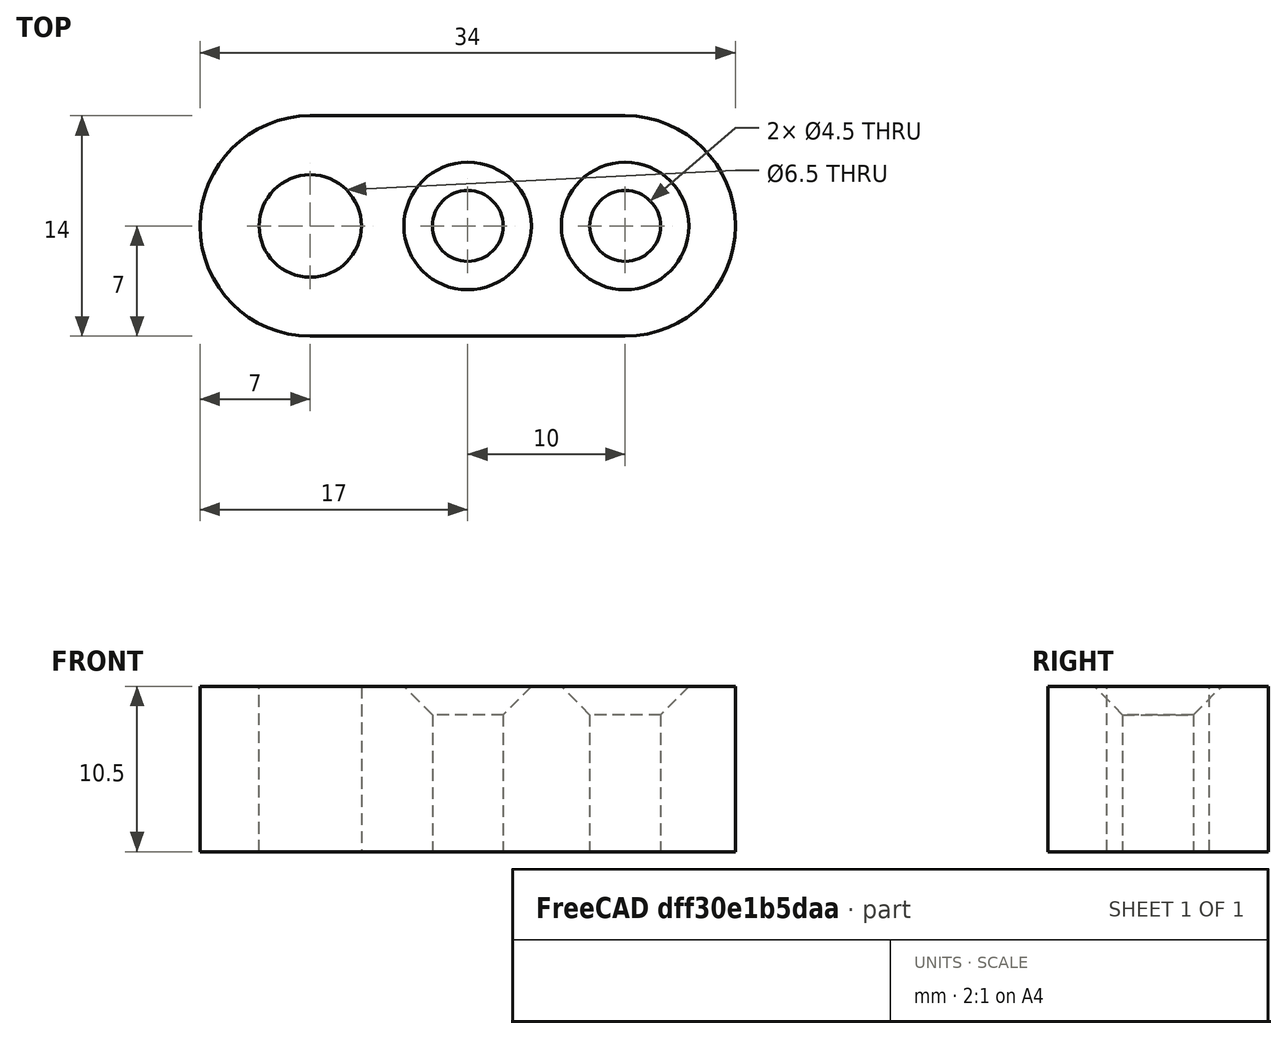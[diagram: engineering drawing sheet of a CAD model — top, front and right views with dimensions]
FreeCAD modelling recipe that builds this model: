
FCSTD DOCUMENT  (FreeCAD 0.19R24267 +99 (Git))
Label: topes
License: All rights reserved
LicenseURL: http://en.wikipedia.org/wiki/All_rights_reserved
objects: Sketcher::SketchObject×3, PartDesign::Pad×1, PartDesign::Hole×1, PartDesign::Pocket×1, PartDesign::Body×1, Mesh::Feature×1
note: 10 computed .brp shape members not serialized (recipe doc carries the construction recipe); baked Part::Feature solids carry a one-line shape summary decoded from their .brp

FEATURE [Sketcher::SketchObject] Sketch
  FullyConstrained = true
  MapMode = 5
  Support = -> [XY_Plane]
  sketch-geometry (4):
    g0: ArcOfCircle CenterX=0 CenterY=0 CenterZ=0 NormalX=0 NormalY=0 NormalZ=1 AngleXU=0 Radius=7 StartAngle=1.5708 EndAngle=4.71239
    g1: ArcOfCircle CenterX=20 CenterY=-4e-16 CenterZ=0 NormalX=0 NormalY=0 NormalZ=1 AngleXU=0 Radius=7 StartAngle=4.71239 EndAngle=7.85398
    g2: LineSegment StartX=-1.3e-15 StartY=-7 StartZ=0 EndX=20 EndY=-7 EndZ=0
    g3: LineSegment StartX=7.66e-14 StartY=7 StartZ=0 EndX=20 EndY=7 EndZ=0
  constraints (9):
    c: Tangent(g0,g3) = 1.5708
    c: Tangent(g0,g2) = -1.5708
    c: Tangent(g2,g1) = -1.5708
    c: Tangent(g3,g1) = 1.5708
    c: Horizontal(g2)
    c: Equal(g0,g1)
    c: Radius(g0) = 7
    c: Coincident(g0,g-1)
    c: DistanceX(g3,g3) = 20
FEATURE [PartDesign::Pad] Pad
  Direction = (1,1,1)
  Length = 10.5
  Length2 = 100
  Profile = -> Sketch
  Type = 0
FEATURE [Sketcher::SketchObject] Sketch001
  FullyConstrained = true
  MapMode = 5
  Placement = pos=(0,0,10.5) rot=(0,0,1;0rad)
  Support = -> [Pad]
  sketch-geometry (2):
    g0: Circle CenterX=10 CenterY=0 CenterZ=0 NormalX=0 NormalY=0 NormalZ=1 AngleXU=0 Radius=2
    g1: Circle CenterX=20 CenterY=0 CenterZ=0 NormalX=0 NormalY=0 NormalZ=1 AngleXU=0 Radius=2
  constraints (6):
    c: PointOnObject(g0,g-1)
    c: Diameter(g0) = 4
    c: Equal(g0,g1) = 4
    c: PointOnObject(g1,g-1)
    c: DistanceX(g0,g1) = 10
    c: DistanceX(g-1,g0) = 10
FEATURE [PartDesign::Hole] Hole
  BaseFeature = -> Pad
  Depth = 25
  DepthType = 1
  Diameter = 4.5
  DrillForDepth = false
  DrillPoint = 1
  DrillPointAngle = 118
  HoleCutCountersinkAngle = 90
  HoleCutCustomValues = false
  HoleCutDepth = 0
  HoleCutDiameter = 8.1
  HoleCutType = 2
  ModelActualThread = false
  Profile = -> Sketch001
  Tapered = false
  TaperedAngle = 90
  ThreadAngle = 60
  ThreadClass = 0
  ThreadCutOffInner = 0.0270633
  ThreadCutOffOuter = 0.0541266
  ThreadDirection = 0
  ThreadFit = 0
  ThreadPitch = 0.25
  ThreadSize = 11
  ThreadType = 1
  Threaded = false
FEATURE [Sketcher::SketchObject] Sketch002
  FullyConstrained = true
  MapMode = 5
  Placement = pos=(0,0,10.5) rot=(0,0,1;0rad)
  Support = -> [Hole]
  sketch-geometry (1):
    g0: Circle CenterX=0 CenterY=0 CenterZ=0 NormalX=0 NormalY=0 NormalZ=1 AngleXU=0 Radius=3.25
  constraints (2):
    c: Coincident(g0,g-1)
    c: Diameter(g0) = 6.5
FEATURE [PartDesign::Pocket] Pocket
  BaseFeature = -> Hole
  Length = 5
  Length2 = 100
  Profile = -> Sketch002
  Type = 1
FEATURE [PartDesign::Body] Body
  Group = -> [Sketch,Pad,Sketch001,Hole,Sketch002,Pocket]
  Origin = -> Origin
  Tip = -> Pocket
FEATURE [Mesh::Feature] Mesh  label="Pocket (Meshed)"
